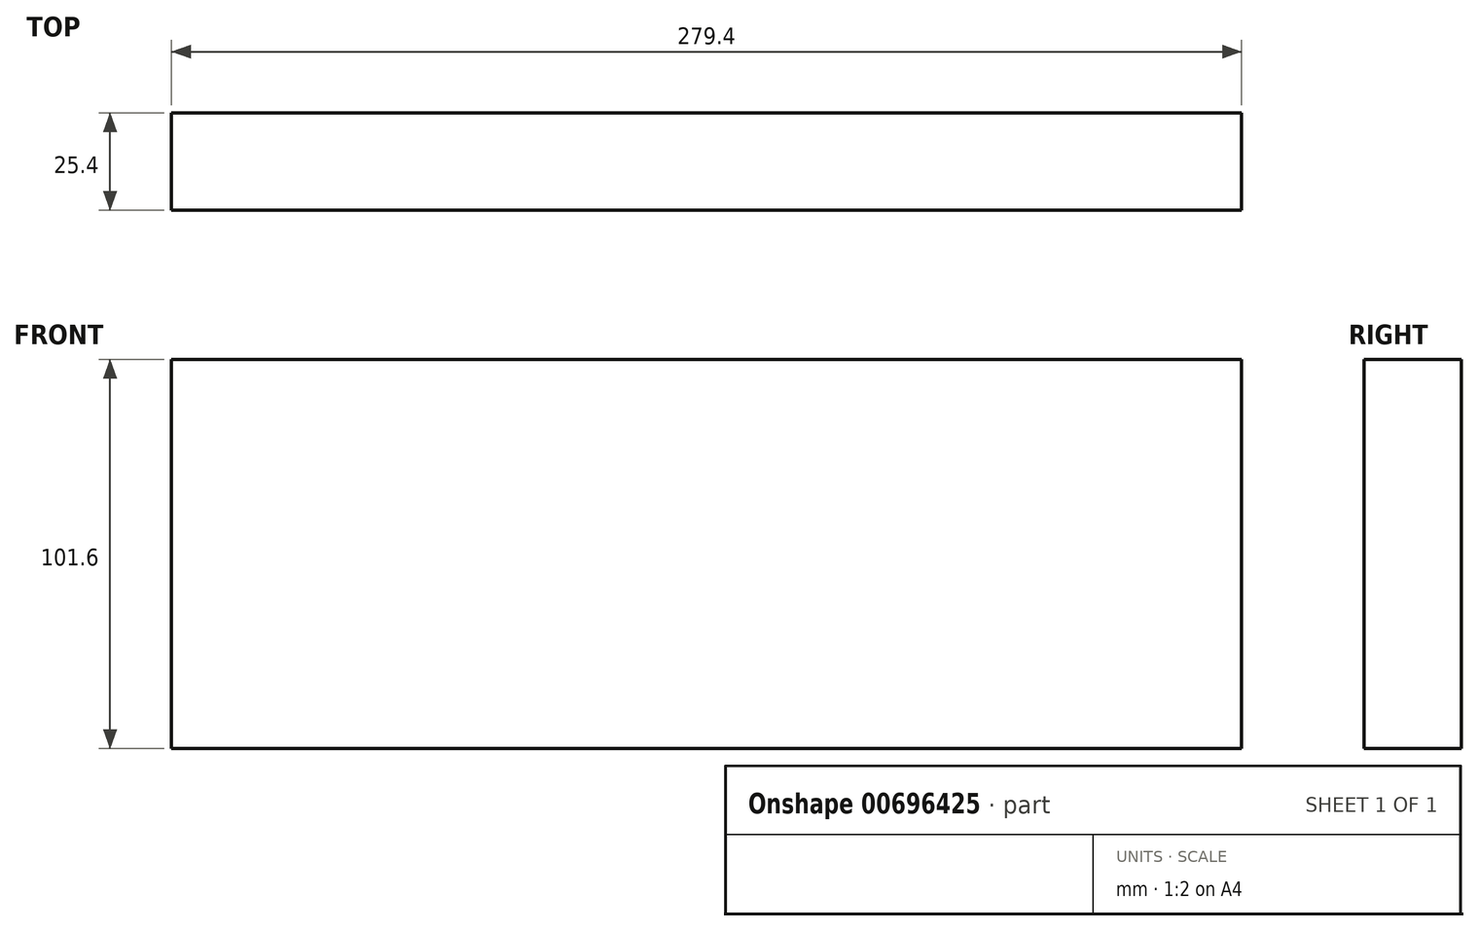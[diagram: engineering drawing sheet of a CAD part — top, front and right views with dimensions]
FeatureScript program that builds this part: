
annotation { "Feature Type Name" : "Feature", "Feature Type Description" : "" }
export const myFeature = defineFeature(function(context is Context, id is Id, definition is map)
    precondition{}
    {
        {
            var Q0;
            Q0=qCreatedBy(makeId("Top.planeOp"),FACE);
            var sketch = newSketch(context, id + "F0", { "sketchPlane" : qUnion([Q0])});
            skLineSegment(sketch, "E0.bottom", {"start": v(-139.7, 0) * mm, "end": v(0, 0) * mm});
            skLineSegment(sketch, "E0.top", {"start": v(-139.7, 25.4) * mm, "end": v(0, 25.4) * mm});
            skLineSegment(sketch, "E0.left", {"start": v(-139.7, 0) * mm, "end": v(-139.7, 25.4) * mm});
            skLineSegment(sketch, "E0.right", {"start": v(0, 0) * mm, "end": v(0, 25.4) * mm});
            skLineSegment(sketch, "E1.MirrorCS", {"start": v(139.7, 25.4) * mm, "end": v(0, 25.4) * mm});
            skLineSegment(sketch, "E2.MirrorCS", {"start": v(139.7, 0) * mm, "end": v(139.7, 25.4) * mm});
            skLineSegment(sketch, "E3.MirrorCS", {"start": v(139.7, 0) * mm, "end": v(0, 0) * mm});
            skSolve(sketch);
        }
        {
            var Q0;
            Q0=makeQuery(id+"F0.imprint","IMPRINT",FACE,{"disambiguationData":[TD([[makeQuery(id+"F0.imprint","IMPRINT",EDGE,{"derivedFrom":sQuery(id+"F0.wireOp",EDGE,"E0.bottom")}),1.0]])]});
            var Q1;
            Q1=makeQuery(id+"F0.imprint","IMPRINT",FACE,{"disambiguationData":[TD([[makeQuery(id+"F0.imprint","IMPRINT",EDGE,{"derivedFrom":sQuery(id+"F0.wireOp",EDGE,"E0.right")}),-1.0]])]});
            extrude(context, id + "F1", {"entities" : qUnion([Q0, Q1]), "depth" : 101.6 * mm, "offsetDistance" : 25.4 * mm});
        }
    });
